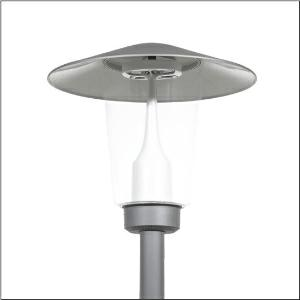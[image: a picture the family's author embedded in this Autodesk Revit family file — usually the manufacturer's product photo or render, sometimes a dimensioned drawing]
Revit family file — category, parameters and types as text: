
# Revit family: pilzleuchte_iq___p1_0a_5xa5235bf14hp_6096
name_source: partatom
category: Lighting Fixtures
units: mm (PartAtom-declared; Revit-internal decimal feet)

## family parameters
Cut with Voids When Loaded = No
Host = Face
Light Source = No
Part Type = Normal
Room Calculation Point = No
Round Connector Dimension = Use Diameter
Shared = No

## types (1)
- --- (1 x LED, 3920 lm, 33.6 W, 2200K)
    Apparent Load = 34 VA
    CIE Flux Codes = 35 64 90 96 100
    Color Rendering = 70
    Color Temperature = 2200K
    Default Elevation = 1800 mm
    Description = Mushroom Luminaire iQ, mast luminaire, Module 540 iQ-SR, primary light control with 3 zone facetted reflector, of plastic, silver coated, highly specular, structured, primary optical cover: cover, of PMMA, transparent, light distribution: P1.0a, light emission: direct distribution, primary light characteristic: strongly asymmetric, installation type: post-top, LED, High Power LED, rated luminous flux: 3.920lm, luminous efficacy: 117lm/W, light colour: 722, colour temperature: 2200K, control gear: ECG iQ, control: pre-setting: logarithmic dimming characteristic, Street-Remote, Auto-Match, Temp-Guard, Lumen-Switch, Night-Set, Smart-Wire, Light-Fading, Desk-Remote (wireless, voltage-free reading and setting of iQ features in the workshop via application-optimized NFC function/RFID function), optimised constant luminous flux control (CLO 2.0), with terminal, 6-pole, max. 2.5mm², mains connection: 230..240V, AC, 50/60Hz, start of lifetime: 34W, end of service life: 36W, reduction: 15W, luminaire housing, upper part, of glass-fibre reinforced polyester, coated, Siteco® metallic grey (DB 702S), diameter: 650mm, height: 586mm, spigot size: d x l = 76 x 70mm (post-top) | with reducer (optional accessory) 60 x 70mm, post-top mast mounting element, of diecast aluminium, coated, Siteco® metallic grey (DB 702S), Module 540 iQ-SR, traffic white (RAL 9016), equipment: Power, protection rating (complete): IP65, insulation class (complete): insulation class II (safety insulation), certification: CE, ENEC, VDE, packaging unit: 1 piece

Light Distribution: P1.0a
    Height = 586 mm
    Lamp = 1 x LED
    Lamp Light Flux = 3920 lm
    Lamp Power = 33.6 W
    Lamp count = 1
    Length = 650 mm
    Luminous efficacy = 117 lm/W
    Manufacturer = Siteco
    ModVariant = No
    Model = 5XA5235BF14HP
    Number of Poles = 1
    OnlyDefault = Yes
    Power Factor = 1
    Product Name = Pilzleuchte iQ | P1.0a
    Product group = mast luminaire | pylon top
    ProductGroupID = 6100
    Protection Class = Protection class II
    Protection Degree = IP 65
    RLX_Detail_Level = 1
    RLX_Emergency_Light_Flux = 0 lm
    RLX_Emergency_Type = 0
    RLX_Emergency_Type_DB = No
    RlxData = <blob elided: 51977 chars, md5=5e2f26c0>
    Socket = socket
    Standby Power = 0 W
    System Light Flux = 3920 lm
    System Power = 34 W
    Type Comments = factory setting: luminous flux: 100 % | dim-lin: 254 | 695 mA
    Type Image = l_1006077.jpg
    URL = http://relux.com
    VarID = @adj_164867
    Voltage = 0 V
    Weight = 0.00 kg
    Width = 0 mm  [stored 0 ft]

note: [stored X ft] marks values corroborated as IEEE doubles in the binary element streams (Revit-internal decimal feet)

## geometry (parser evidence)
native form markers: Blend x4, Sweep x11
no freeform markers — native parametric forms only
